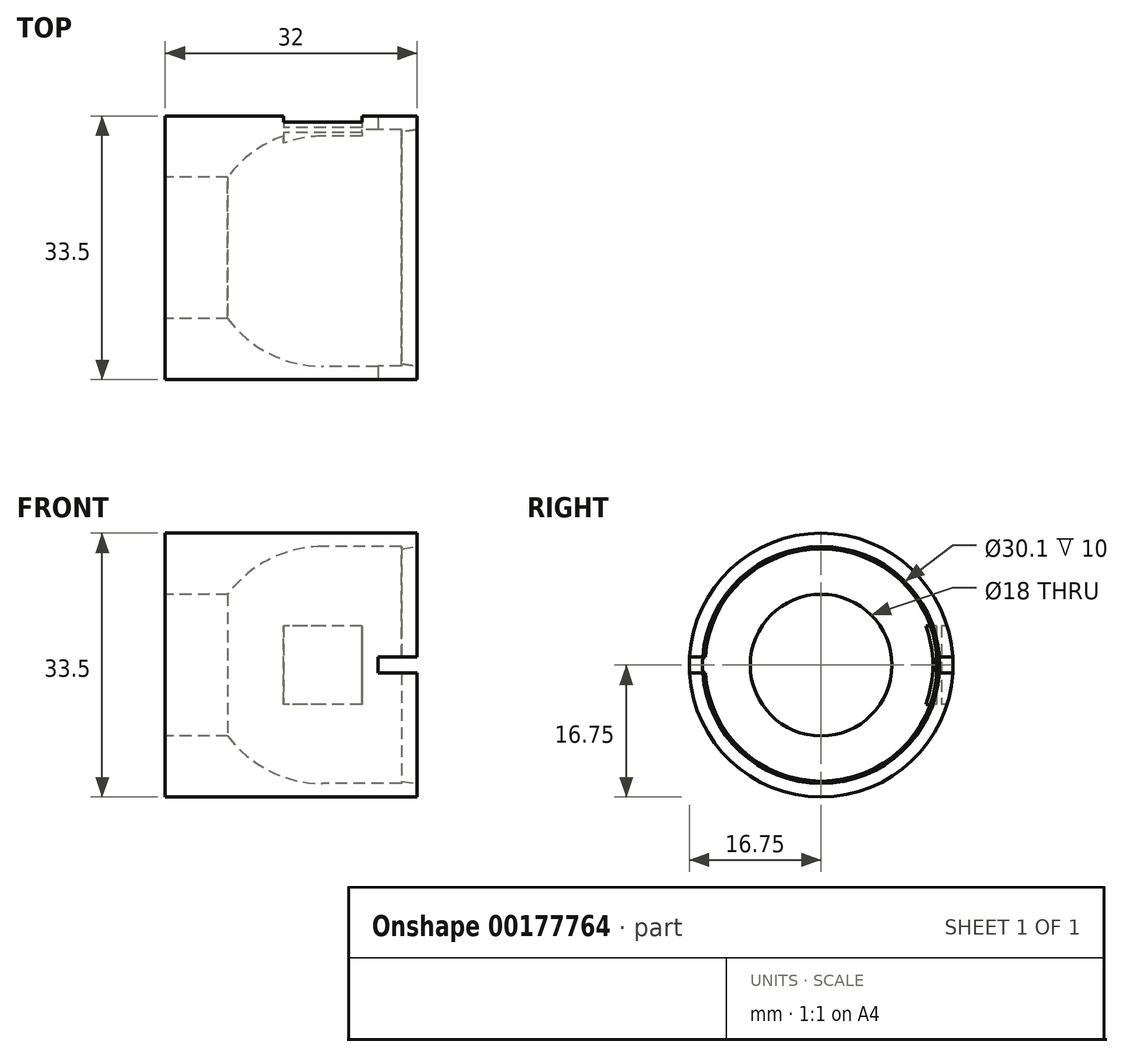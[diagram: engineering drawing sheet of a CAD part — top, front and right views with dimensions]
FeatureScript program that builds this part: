
annotation { "Feature Type Name" : "Feature", "Feature Type Description" : "" }
export const myFeature = defineFeature(function(context is Context, id is Id, definition is map)
    precondition{}
    {
        {
            var Q0;
            Q0=qCreatedBy(makeId("Front.planeOp"),FACE);
            var sketch = newSketch(context, id + "F0", { "sketchPlane" : qUnion([Q0])});
            skLineSegment(sketch, "E0", {"start": v(0, 0) * mm, "end": v(20.47, 0) * mm, "construction": true});
            skLineSegment(sketch, "E1", {"start": v(10, 15.05) * mm, "end": v(0, 15.05) * mm});
            skArc(sketch, "E2", {"start": v(0, 15.05) * mm, "mid": v(-6.75, 13.45) * mm, "end": v(-12.06, 9) * mm});
            skLineSegment(sketch, "E3", {"start": v(-12.06, 9) * mm, "end": v(-20, 9) * mm});
            skLineSegment(sketch, "E4", {"start": v(-20, 9) * mm, "end": v(-20, 16.75) * mm});
            skLineSegment(sketch, "E5", {"start": v(-20, 16.75) * mm, "end": v(12, 16.75) * mm});
            skLineSegment(sketch, "E6", {"start": v(12, 16.75) * mm, "end": v(12, 15.05) * mm});
            skLineSegment(sketch, "E7", {"start": v(12, 15.05) * mm, "end": v(10, 14.75) * mm});
            skLineSegment(sketch, "E8", {"start": v(10, 14.75) * mm, "end": v(10, 15.05) * mm});
            skSolve(sketch);
        }
        {
            var Q0;
            Q0 = qSketchRegion(id + "F0", true);
            var Q1;
            Q1=sQuery(id+"F0.wireOp",EDGE,"E0");
            revolve(context, id + "F1", {"entities" : qUnion([Q0]), "axis" : qUnion([Q1]), "revolveType" : RevolveType.FULL});
        }
        {
            var Q0;
            Q0=qCreatedBy(makeId("Front.planeOp"),FACE);
            var sketch = newSketch(context, id + "F2", { "sketchPlane" : qUnion([Q0])});
            skLineSegment(sketch, "E9", {"start": v(0, 0) * mm, "end": v(14.6, 0) * mm, "construction": true});
            skLineSegment(sketch, "E10.bottom", {"start": v(17, -1) * mm, "end": v(7, -1) * mm});
            skLineSegment(sketch, "E10.top", {"start": v(17, 1) * mm, "end": v(7, 1) * mm});
            skLineSegment(sketch, "E10.left", {"start": v(17, -1) * mm, "end": v(17, 1) * mm});
            skLineSegment(sketch, "E10.right", {"start": v(7, -1) * mm, "end": v(7, 1) * mm});
            skPoint(sketch, "E10.middle", {"position": v(12, 0) * mm});
            skSolve(sketch);
        }
        {
            var Q0;
            Q0 = qSketchRegion(id + "F2", true);
            extrude(context, id + "F3", {"entities" : qUnion([Q0]), "operationType" : NewBodyOperationType.REMOVE, "endBound" : BoundingType.THROUGH_ALL, "oppositeDirection" : true, "depth" : 25 * mm, "hasSecondDirection" : true, "secondDirectionBound" : SecondDirectionBoundingType.THROUGH_ALL, "secondDirectionOppositeDirection" : false, "secondDirectionDepth" : 25 * mm});
        }
        {
            var Q0;
            Q0=qCreatedBy(makeId("Front.planeOp"),FACE);
            var sketch = newSketch(context, id + "F4", { "sketchPlane" : qUnion([Q0])});
            skLineSegment(sketch, "E11.bottom", {"start": v(5, -5) * mm, "end": v(-5, -5) * mm});
            skLineSegment(sketch, "E11.top", {"start": v(5, 5) * mm, "end": v(-5, 5) * mm});
            skLineSegment(sketch, "E11.left", {"start": v(5, -5) * mm, "end": v(5, 5) * mm});
            skLineSegment(sketch, "E11.right", {"start": v(-5, -5) * mm, "end": v(-5, 5) * mm});
            skPoint(sketch, "E11.middle", {"position": v(0, 0) * mm});
            skSolve(sketch);
        }
        {
            var Q0;
            Q0 = qSketchRegion(id + "F4", true);
            extrude(context, id + "F5", {"entities" : qUnion([Q0]), "operationType" : NewBodyOperationType.REMOVE, "oppositeDirection" : true, "depth" : 25 * mm});
        }
        {
            var Q0;
            Q0=makeQuery(id+"F5.boolean.opBoolean","COPY",FACE,{"derivedFrom":makeQuery(id+"F5.opExtrude","SWEPT_FACE",FACE,{"disambiguationData":[OSD([sQuery(id+"F4.wireOp",EDGE,"E11.right")])]})});
            var sketch = newSketch(context, id + "F6", { "sketchPlane" : qUnion([Q0])});
            skLineSegment(sketch, "E12.bottom", {"start": v(14.64, 5) * mm, "end": v(15.29, 5) * mm});
            skLineSegment(sketch, "E12.top", {"start": v(14.64, -5) * mm, "end": v(15.29, -5) * mm});
            skLineSegment(sketch, "E12.left", {"start": v(14.64, 5) * mm, "end": v(14.64, -5) * mm});
            skLineSegment(sketch, "E12.right", {"start": v(15.29, 5) * mm, "end": v(15.29, -5) * mm});
            skSolve(sketch);
        }
        {
            var Q0;
            Q0 = qSketchRegion(id + "F6", true);
            var Q1;
            Q1=makeQuery(id+"F5.boolean.opBoolean","COPY",FACE,{"derivedFrom":makeQuery(id+"F5.opExtrude","SWEPT_FACE",FACE,{"disambiguationData":[OSD([sQuery(id+"F4.wireOp",EDGE,"E11.left")])]})});
            extrude(context, id + "F7", {"entities" : qUnion([Q0]), "operationType" : NewBodyOperationType.ADD, "endBound" : BoundingType.UP_TO_SURFACE, "endBoundEntityFace" : qUnion([Q1]), "depth" : 25 * mm});
        }
    });
